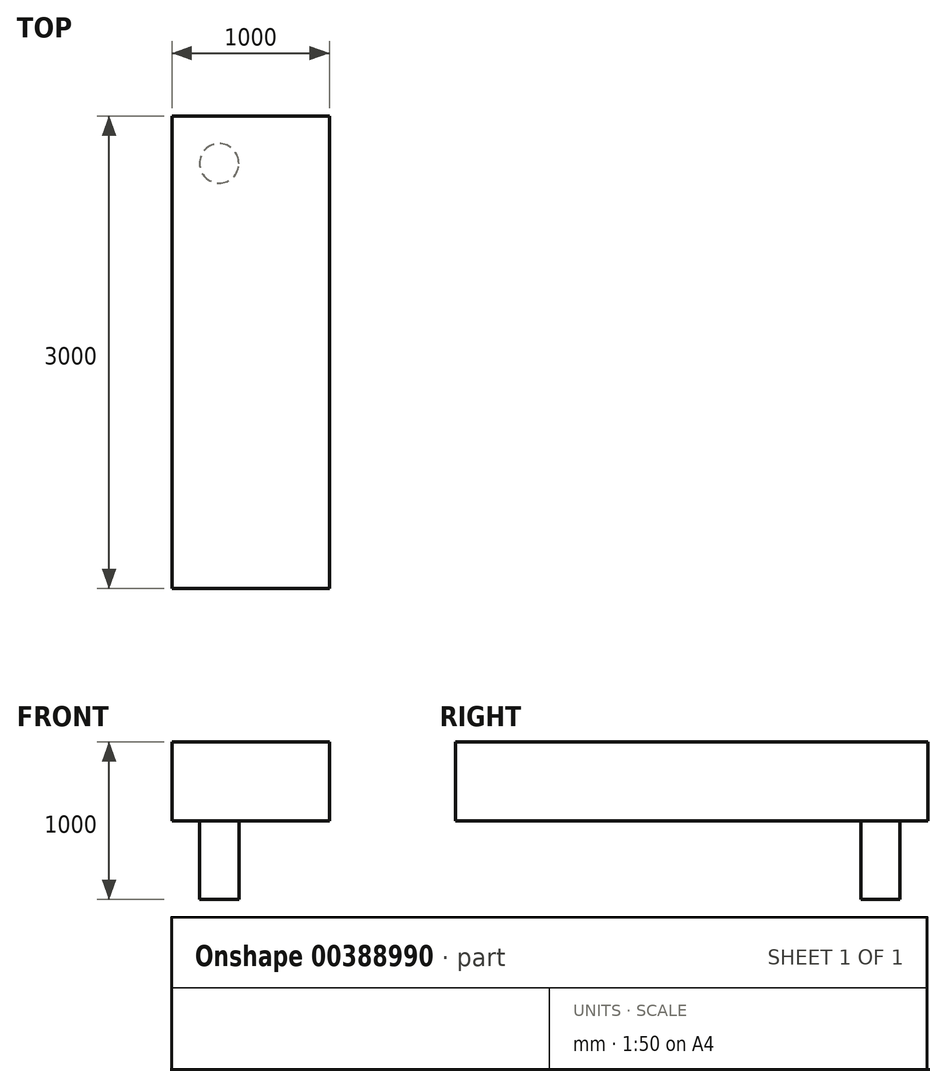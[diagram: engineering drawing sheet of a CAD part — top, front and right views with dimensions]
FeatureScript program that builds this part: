
annotation { "Feature Type Name" : "Feature", "Feature Type Description" : "" }
export const myFeature = defineFeature(function(context is Context, id is Id, definition is map)
    precondition{}
    {
        {
            var Q0;
            Q0=qCreatedBy(makeId("Front.planeOp"),FACE);
            var sketch = newSketch(context, id + "F0", { "sketchPlane" : qUnion([Q0])});
            skLineSegment(sketch, "E0.bottom", {"start": v(0, 0) * mm, "end": v(1000, 0) * mm});
            skLineSegment(sketch, "E0.top", {"start": v(0, 500) * mm, "end": v(1000, 500) * mm});
            skLineSegment(sketch, "E0.left", {"start": v(0, 0) * mm, "end": v(0, 500) * mm});
            skLineSegment(sketch, "E0.right", {"start": v(1000, 0) * mm, "end": v(1000, 500) * mm});
            skSolve(sketch);
        }
        {
            var Q0;
            Q0 = qSketchRegion(id + "F0", true);
            extrude(context, id + "F1", {"entities" : qUnion([Q0]), "depth" : 3000 * mm});
        }
        {
            var Q0;
            Q0=qCreatedBy(makeId("Top.planeOp"),FACE);
            var sketch = newSketch(context, id + "F2", { "sketchPlane" : qUnion([Q0])});
            skCircle(sketch, "E1", {"center": v(300, -300) * mm, "radius": 125 * mm});
            skSolve(sketch);
        }
        {
            var Q0;
            Q0 = qSketchRegion(id + "F2", true);
            extrude(context, id + "F3", {"entities" : qUnion([Q0]), "operationType" : NewBodyOperationType.ADD, "oppositeDirection" : true, "depth" : 500 * mm});
        }
    });
